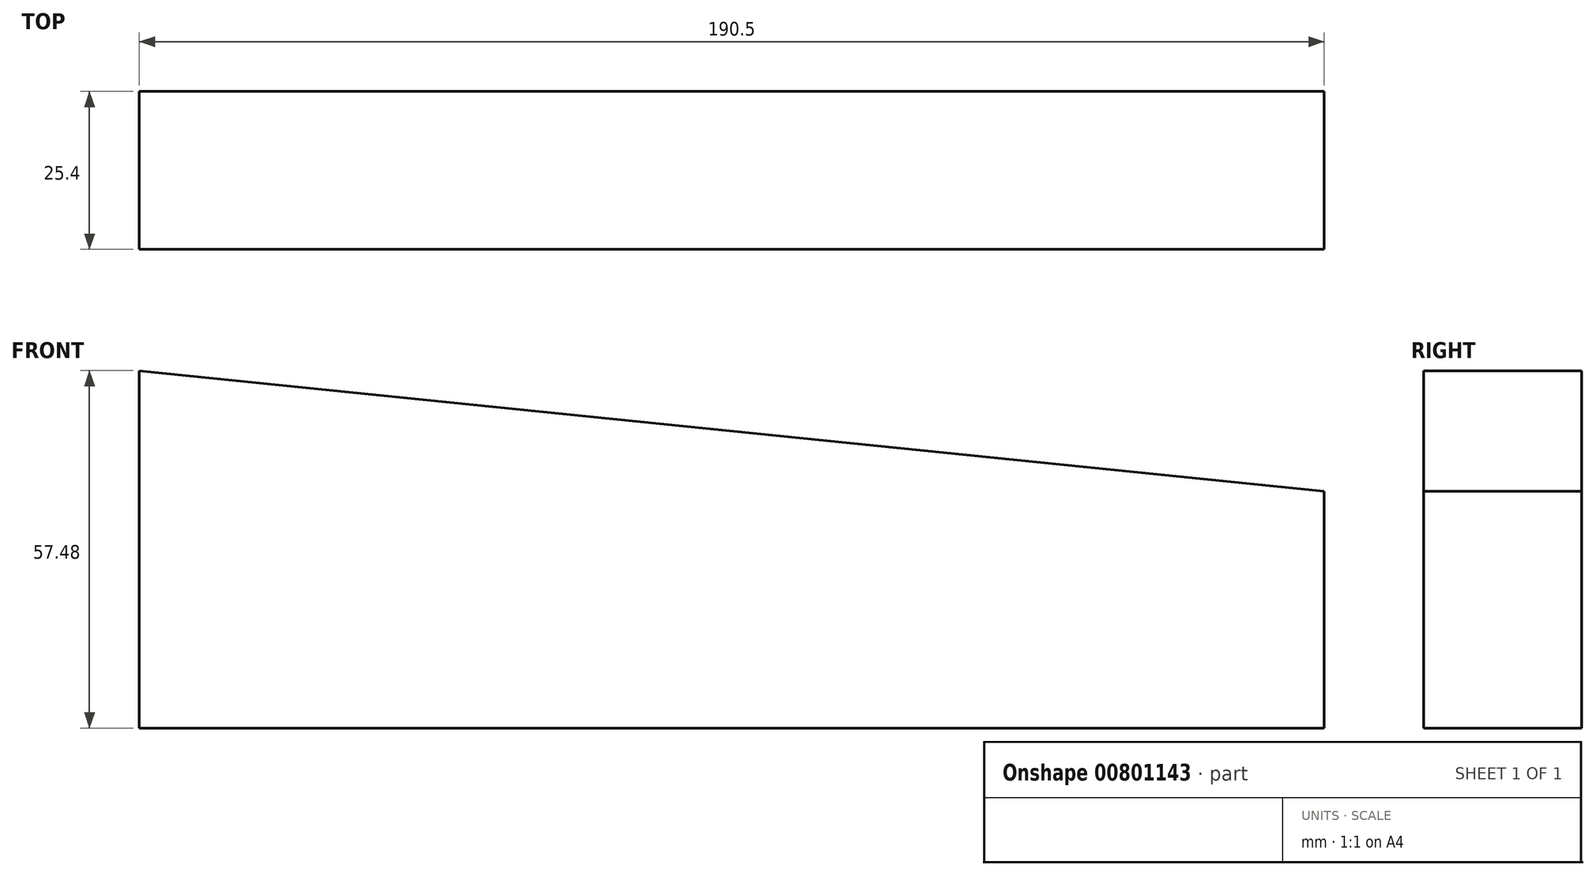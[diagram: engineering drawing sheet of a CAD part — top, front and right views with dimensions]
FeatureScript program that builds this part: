
annotation { "Feature Type Name" : "Feature", "Feature Type Description" : "" }
export const myFeature = defineFeature(function(context is Context, id is Id, definition is map)
    precondition{}
    {
        {
            var Q0;
            Q0=qCreatedBy(makeId("Front.planeOp"),FACE);
            var sketch = newSketch(context, id + "F0", { "sketchPlane" : qUnion([Q0])});
            skLineSegment(sketch, "E0", {"start": v(0, 0) * mm, "end": v(0, 57.48) * mm});
            skLineSegment(sketch, "E1", {"start": v(0, 0) * mm, "end": v(190.5, 0) * mm});
            skLineSegment(sketch, "E2", {"start": v(190.5, 0) * mm, "end": v(190.5, 38.1) * mm});
            skLineSegment(sketch, "E3", {"start": v(190.5, 38.1) * mm, "end": v(0, 57.48) * mm});
            skSolve(sketch);
        }
        {
            var Q0;
            Q0=makeQuery(id+"F0.imprint","IMPRINT",FACE,{"disambiguationData":[TD([[makeQuery(id+"F0.imprint","IMPRINT",EDGE,{"derivedFrom":sQuery(id+"F0.wireOp",EDGE,"E0")}),-1.0]])]});
            extrude(context, id + "F1", {"entities" : qUnion([Q0]), "depth" : 25.4 * mm, "offsetDistance" : 25.4 * mm});
        }
    });
